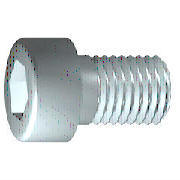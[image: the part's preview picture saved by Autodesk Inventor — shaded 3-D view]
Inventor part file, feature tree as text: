
AUTODESK INVENTOR PART (.ipt)
format: ipt  version: 2023.5 (Build 275446000, 446)  size: 180,736 bytes
history: native  units: mm (DEFAULTED — no unit token found)
features: extrude x1, plane x1, fillet x1
ambient origin geometry x7: Origin, YZ Plane, XY Plane, X Axis, Y Axis, Z Axis, Center Point
bodies: Solid1 (feature_tree), Body (feature_tree)
feature tree (3):
  extrude  "Slot"  Depth=25.4mm
  plane  "Work Plane1"
  fillet  "Fillet2"  Radius=2.5401mm
